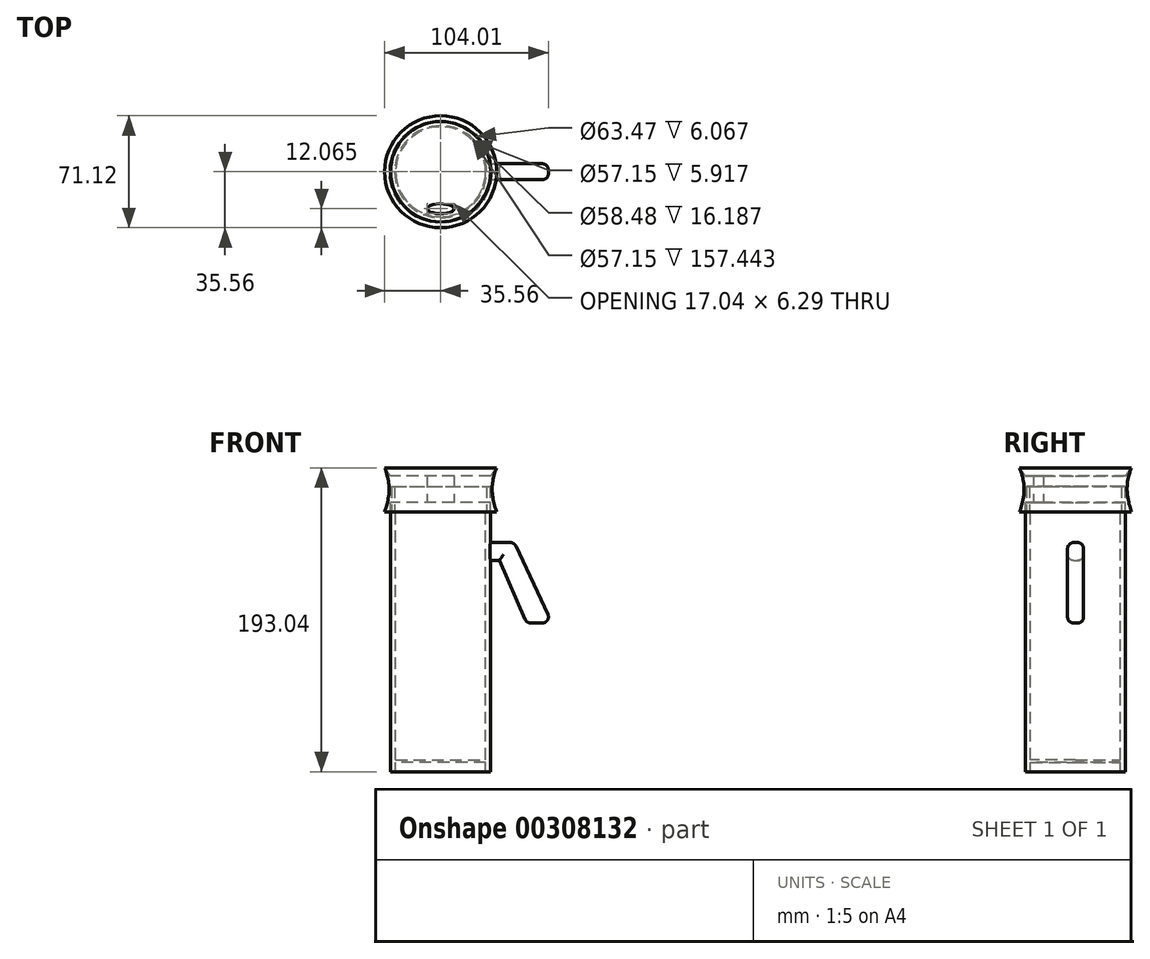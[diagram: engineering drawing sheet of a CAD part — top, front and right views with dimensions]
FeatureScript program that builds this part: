
annotation { "Feature Type Name" : "Feature", "Feature Type Description" : "" }
export const myFeature = defineFeature(function(context is Context, id is Id, definition is map)
    precondition{}
    {
        {
            var Q0;
            Q0=qCreatedBy(makeId("Top.planeOp"),FACE);
            var sketch = newSketch(context, id + "F0", { "sketchPlane" : qUnion([Q0])});
            skCircle(sketch, "E0", {"center": v(0, 0) * mm, "radius": 31.75 * mm});
            skCircle(sketch, "E1", {"center": v(0, 0) * mm, "radius": 28.58 * mm});
            skSolve(sketch);
        }
        {
            var Q0;
            Q0=makeQuery(id+"F0.imprint","IMPRINT",FACE,{"disambiguationData":[TD([[makeQuery(id+"F0.imprint","IMPRINT",EDGE,{"derivedFrom":sQuery(id+"F0.wireOp",EDGE,"E0")}),1.0]])]});
            extrude(context, id + "F1", {"entities" : qUnion([Q0]), "oppositeDirection" : true, "depth" : 165.1 * mm});
        }
        {
            var Q0;
            Q0=qCreatedBy(makeId("Front.planeOp"),FACE);
            var sketch = newSketch(context, id + "F2", { "sketchPlane" : qUnion([Q0])});
            skLineSegment(sketch, "E2", {"start": v(0, 0) * mm, "end": v(35.56, 0) * mm});
            skLineSegment(sketch, "E3", {"start": v(35.56, 27.94) * mm, "end": v(0, 27.94) * mm});
            skFitSpline(sketch, "E4", {"points": [v(35.56, 0) * mm, v(35.56, 27.94) * mm], "startDerivative": vector(-11.39, 32.99) * mm, "endDerivative": vector(11.39, 29.01) * mm});
            skLineSegment(sketch, "E5", {"start": v(-0.02, 0) * mm, "end": v(-0.02, 6.07) * mm});
            skLineSegment(sketch, "E6", {"start": v(-0.02, 6.07) * mm, "end": v(31.73, 6.07) * mm});
            skLineSegment(sketch, "E7", {"start": v(31.73, 6.07) * mm, "end": v(31.73, 0) * mm});
            skLineSegment(sketch, "E8", {"start": v(0, 27.94) * mm, "end": v(0, 0) * mm});
            skLineSegment(sketch, "E9", {"start": v(35.56, 27.94) * mm, "end": v(31.9, 22.86) * mm});
            skLineSegment(sketch, "E10", {"start": v(31.9, 22.86) * mm, "end": v(0, 22.86) * mm});
            skSolve(sketch);
        }
        {
            var Q0;
            {var subQ4=sQuery(id+"F2.wireOp",EDGE,"E4");Q0=makeQuery(id+"F2.imprint","IMPRINT",FACE,{"disambiguationData":[TD([[makeQuery(id+"F2.imprint","IMPRINT",EDGE,{"derivedFrom":subQ4}),1.0]])]});}
            var Q1;
            Q1=sQuery(id+"F2.wireOp",EDGE,"E8");
            revolve(context, id + "F3", {"entities" : qUnion([Q0]), "axis" : qUnion([Q1]), "revolveType" : RevolveType.FULL});
        }
        {
            var Q0;
            Q0=qCreatedBy(makeId("Top.planeOp"),FACE);
            var sketch = newSketch(context, id + "F4", { "sketchPlane" : qUnion([Q0])});
            skEllipse(sketch, "E11", {"center": v(0, -23.5) * mm, "majorRadius": 8.52 * mm, "minorRadius": 3.15 * mm, "majorAxis": v(1, 0)});
            skSolve(sketch);
        }
        {
            var Q0;
            Q0=makeQuery(id+"F4.imprint","IMPRINT",FACE,{"disambiguationData":[TD([[makeQuery(id+"F4.imprint","IMPRINT",EDGE,{"derivedFrom":sQuery(id+"F4.wireOp",EDGE,"E11")}),1.0]])]});
            extrude(context, id + "F5", {"entities" : qUnion([Q0]), "operationType" : NewBodyOperationType.REMOVE, "depth" : 22.86 * mm});
        }
        {
            var Q0;
            Q0=qCreatedBy(makeId("Front.planeOp"),FACE);
            var sketch = newSketch(context, id + "F6", { "sketchPlane" : qUnion([Q0])});
            skLineSegment(sketch, "E12", {"start": v(31.26, 16.19) * mm, "end": v(31.26, -159.18) * mm});
            skLineSegment(sketch, "E13", {"start": v(31.26, -159.18) * mm, "end": v(0, -159.18) * mm});
            skLineSegment(sketch, "E14", {"start": v(0, -159.18) * mm, "end": v(0, 16.19) * mm});
            skLineSegment(sketch, "E15", {"start": v(0, 16.19) * mm, "end": v(31.26, 16.19) * mm});
            skLineSegment(sketch, "E16", {"start": v(0, -157.44) * mm, "end": v(29.24, -157.44) * mm});
            skLineSegment(sketch, "E17", {"start": v(29.24, -157.44) * mm, "end": v(29.24, 16.19) * mm});
            skLineSegment(sketch, "E18", {"start": v(29.24, 16.19) * mm, "end": v(29.24, -19.53) * mm});
            skLineSegment(sketch, "E19", {"start": v(29.24, -19.53) * mm, "end": v(29.24, -30.91) * mm});
            skLineSegment(sketch, "E20", {"start": v(29.24, -19.53) * mm, "end": v(46.8, -19.53) * mm});
            skLineSegment(sketch, "E21", {"start": v(29.24, -30.91) * mm, "end": v(37.4, -30.91) * mm});
            skPoint(sketch, "E22.endSnap0", {"position": v(29.24, -70.63) * mm});
            skLineSegment(sketch, "E23", {"start": v(46.8, -19.53) * mm, "end": v(70.62, -70.63) * mm});
            skLineSegment(sketch, "E24", {"start": v(70.62, -70.63) * mm, "end": v(54.73, -70.63) * mm});
            skLineSegment(sketch, "E25", {"start": v(54.73, -70.63) * mm, "end": v(37.4, -30.91) * mm});
            skSolve(sketch);
        }
        {
            var Q0;
            Q0=makeQuery(id+"F6.imprint","IMPRINT",FACE,{"disambiguationData":[TD([[makeQuery(id+"F6.imprint","IMPRINT",EDGE,{"derivedFrom":sQuery(id+"F6.wireOp",EDGE,"E12")}),-1.0]])]});
            var Q1;
            {var subQ1=sQuery(id+"F6.wireOp",EDGE,"E13");Q1=makeQuery(id+"F6.imprint","IMPRINT",FACE,{"disambiguationData":[TD([[makeQuery(id+"F6.imprint","IMPRINT",EDGE,{"derivedFrom":subQ1}),-1.0]])]});}
            var Q2;
            Q2=sQuery(id+"F6.wireOp",EDGE,"E14");
            revolve(context, id + "F7", {"entities" : qUnion([Q0, Q1]), "axis" : qUnion([Q2]), "revolveType" : RevolveType.FULL});
        }
        {
            var Q0;
            {var subQ5=sQuery(id+"F6.wireOp",EDGE,"E19");Q0=makeQuery(id+"F6.imprint","IMPRINT",FACE,{"disambiguationData":[TD([[makeQuery(id+"F6.imprint","IMPRINT",EDGE,{"derivedFrom":subQ5}),1.0]])]});}
            var Q1;
            {var subQ4=sQuery(id+"F6.wireOp",EDGE,"E23");Q1=makeQuery(id+"F6.imprint","IMPRINT",FACE,{"disambiguationData":[TD([[makeQuery(id+"F6.imprint","IMPRINT",EDGE,{"derivedFrom":subQ4}),-1.0]])]});}
            extrude(context, id + "F8", {"entities" : qUnion([Q0, Q1]), "operationType" : NewBodyOperationType.ADD, "endBound" : BoundingType.SYMMETRIC, "depth" : 10.16 * mm});
        }
        {
            var Q0;
            Q0=makeQuery(id+"F8.opExtrude","CAP_EDGE",EDGE,{"disambiguationData":[OSD([sQuery(id+"F6.wireOp",EDGE,"E20")])],"isStart":false});
            var Q1;
            Q1=makeQuery(id+"F8.opExtrude","CAP_EDGE",EDGE,{"disambiguationData":[OSD([sQuery(id+"F6.wireOp",EDGE,"E21")])],"isStart":false});
            var Q2;
            Q2=makeQuery(id+"F8.opExtrude","CAP_EDGE",EDGE,{"disambiguationData":[OSD([sQuery(id+"F6.wireOp",EDGE,"E25")])],"isStart":false});
            var Q3;
            Q3=makeQuery(id+"F8.opExtrude","CAP_EDGE",EDGE,{"disambiguationData":[OSD([sQuery(id+"F6.wireOp",EDGE,"E20")])],"isStart":true});
            var Q4;
            Q4=makeQuery(id+"F8.opExtrude","SWEPT_FACE",FACE,{"disambiguationData":[OSD([sQuery(id+"F6.wireOp",EDGE,"E23")])]});
            var Q5;
            Q5=makeQuery(id+"F8.opExtrude","CAP_EDGE",EDGE,{"disambiguationData":[OSD([sQuery(id+"F6.wireOp",EDGE,"E24")])],"isStart":false});
            var Q6;
            Q6=makeQuery(id+"F8.boolean.opBoolean","INTERSECT",EDGE,{"derivedFrom":[makeQuery(id+"F7.opRevolve","SWEPT_FACE",FACE,{"disambiguationData":[OSD([sQuery(id+"F6.wireOp",EDGE,"E12")])]}),makeQuery(id+"F8.opExtrude","CAP_FACE",FACE,{"disambiguationData":[OSD([sQuery(id+"F6.wireOp",EDGE,"E19"),sQuery(id+"F6.wireOp",EDGE,"E20"),sQuery(id+"F6.wireOp",EDGE,"E21"),sQuery(id+"F6.wireOp",EDGE,"E23"),sQuery(id+"F6.wireOp",EDGE,"E24"),sQuery(id+"F6.wireOp",EDGE,"E25")])],"isStart":false})]});
            var Q7;
            Q7=makeQuery(id+"F8.opExtrude","CAP_EDGE",EDGE,{"disambiguationData":[OSD([sQuery(id+"F6.wireOp",EDGE,"E21")])],"isStart":true});
            var Q8;
            Q8=makeQuery(id+"F8.opExtrude","SWEPT_FACE",FACE,{"disambiguationData":[OSD([sQuery(id+"F6.wireOp",EDGE,"E24")])]});
            var Q9;
            Q9=makeQuery(id+"F8.opExtrude","CAP_EDGE",EDGE,{"disambiguationData":[OSD([sQuery(id+"F6.wireOp",EDGE,"E25")])],"isStart":true});
            fillet(context, id + "F9", {"entities" : qUnion([Q0, Q1, Q2, Q3, Q4, Q5, Q6, Q7, Q8, Q9]), "radius" : 3.8 * mm, "tangentPropagation" : true, "allowEdgeOverflow" : false});
        }
    });
